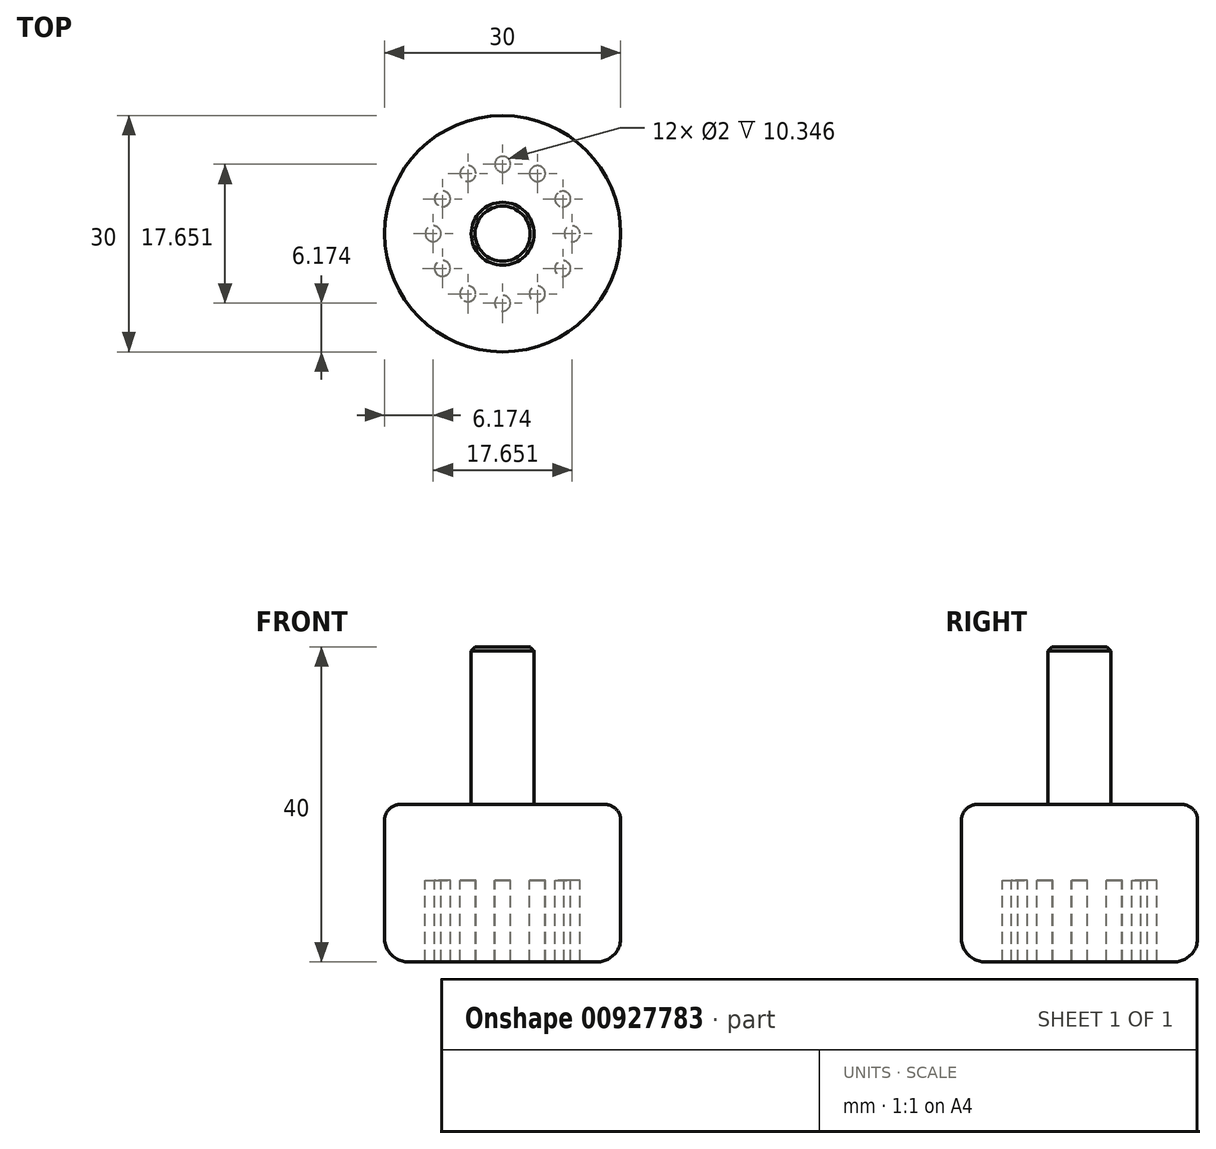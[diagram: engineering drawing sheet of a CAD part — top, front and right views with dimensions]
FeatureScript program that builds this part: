
annotation { "Feature Type Name" : "Feature", "Feature Type Description" : "" }
export const myFeature = defineFeature(function(context is Context, id is Id, definition is map)
    precondition{}
    {
        {
            var Q0;
            Q0=qCreatedBy(makeId("Top.planeOp"),FACE);
            cPlane(context, id + "F0", {"entities" : qUnion([Q0]), "cplaneType" : CPlaneType.OFFSET, "offset" : 83.57 * mm, "width" : 152.4 * mm, "height" : 152.4 * mm});
        }
        {
            var Q0;
            Q0=qCreatedBy(makeId("Front.planeOp"),FACE);
            var sketch = newSketch(context, id + "F1", { "sketchPlane" : qUnion([Q0])});
            skLineSegment(sketch, "E0", {"start": v(8.85, 83.91) * mm, "end": v(8.85, 47.77) * mm});
            skSolve(sketch);
        }
        {
            var Q0;
            Q0=qCreatedBy(id+"F0.planeOp",FACE);
            var sketch = newSketch(context, id + "F2", { "sketchPlane" : qUnion([Q0])});
            skCircle(sketch, "E1", {"center": v(8.83, -0.01) * mm, "radius": 1 * mm});
            skSolve(sketch);
        }
        {
            var Q0;
            Q0=makeQuery(id+"F2.imprint","IMPRINT",FACE,{"disambiguationData":[TD([[makeQuery(id+"F2.imprint","IMPRINT",EDGE,{"derivedFrom":sQuery(id+"F2.wireOp",EDGE,"E1")}),1.0]])]});
            var Q1;
            Q1=sQuery(id+"F1.wireOp",EDGE,"E0");
            var Q2;
            Q2=sQuery(id+"F1.wireOp",EDGE,"10137925-59a1-47c4-baab-5b0ec24871b5");
            sweep(context, id + "F3", {"profiles" : qUnion([Q0]), "path" : qUnion([Q1, Q2])});
        }
        {
            var Q0;
            Q0=qCreatedBy(makeId("Front.planeOp"),FACE);
            var sketch = newSketch(context, id + "F4", { "sketchPlane" : qUnion([Q0])});
            skLineSegment(sketch, "E2", {"start": v(0, 0) * mm, "end": v(0, 81.13) * mm, "construction": true});
            skSolve(sketch);
        }
        {
            var Q0;
            Q0=makeQuery(id+"F3.opSweep","SWEPT_BODY",BODY,{"disambiguationData":[OSD([sQuery(id+"F1.wireOp",EDGE,"10137925-59a1-47c4-baab-5b0ec24871b5"),sQuery(id+"F2.wireOp",EDGE,"E1")])]});
            var Q1;
            Q1=sQuery(id+"F4.wireOp",EDGE,"E2");
            circularPattern(context, id + "F5", {"entities" : qUnion([Q0]), "axis" : qUnion([Q1]), "angle" : 360 * degree, "instanceCount" : 12, "equalSpace" : true});
        }
        {
            var Q0;
            Q0=qCreatedBy(id+"F0.planeOp",FACE);
            var sketch = newSketch(context, id + "F6", { "sketchPlane" : qUnion([Q0])});
            skCircle(sketch, "E3", {"center": v(0, 0) * mm, "radius": 15 * mm});
            skSolve(sketch);
        }
        {
            var Q0;
            Q0=makeQuery(id+"F6.imprint","IMPRINT",FACE,{"disambiguationData":[TD([[makeQuery(id+"F6.imprint","IMPRINT",EDGE,{"derivedFrom":sQuery(id+"F6.wireOp",EDGE,"E3")}),1.0]])]});
            extrude(context, id + "F7", {"entities" : qUnion([Q0]), "endBound" : BoundingType.SYMMETRIC, "depth" : 20 * mm, "offsetDistance" : 25 * mm});
        }
        {
            var Q0;
            Q0=makeQuery(id+"F7.opExtrude","CAP_EDGE",EDGE,{"disambiguationData":[OSD([sQuery(id+"F6.wireOp",EDGE,"E3")])],"isStart":true});
            fillet(context, id + "F8", {"entities" : qUnion([Q0]), "radius" : 3 * mm, "tangentPropagation" : true, "allowEdgeOverflow" : false});
        }
        {
            var Q0;
            Q0=makeQuery(id+"F7.opExtrude","CAP_EDGE",EDGE,{"disambiguationData":[OSD([sQuery(id+"F6.wireOp",EDGE,"E3")])],"isStart":false});
            fillet(context, id + "F9", {"entities" : qUnion([Q0]), "radius" : 2 * mm, "tangentPropagation" : true, "allowEdgeOverflow" : false});
        }
        {
            var Q0;
            Q0=makeQuery(id+"F3.opSweep","SWEPT_BODY",BODY,{"disambiguationData":[OSD([sQuery(id+"F1.wireOp",EDGE,"E0"),sQuery(id+"F2.wireOp",EDGE,"E1")])]});
            var Q1;
            Q1=makeQuery(id+"F5.opPattern","COPY",BODY,{"derivedFrom":makeQuery(id+"F3.opSweep","SWEPT_BODY",BODY,{"disambiguationData":[OSD([sQuery(id+"F1.wireOp",EDGE,"E0"),sQuery(id+"F2.wireOp",EDGE,"E1")])]}),"instanceName":"1"});
            var Q2;
            Q2=makeQuery(id+"F5.opPattern","COPY",BODY,{"derivedFrom":makeQuery(id+"F3.opSweep","SWEPT_BODY",BODY,{"disambiguationData":[OSD([sQuery(id+"F1.wireOp",EDGE,"E0"),sQuery(id+"F2.wireOp",EDGE,"E1")])]}),"instanceName":"2"});
            var Q3;
            Q3=makeQuery(id+"F5.opPattern","COPY",BODY,{"derivedFrom":makeQuery(id+"F3.opSweep","SWEPT_BODY",BODY,{"disambiguationData":[OSD([sQuery(id+"F1.wireOp",EDGE,"E0"),sQuery(id+"F2.wireOp",EDGE,"E1")])]}),"instanceName":"3"});
            var Q4;
            Q4=makeQuery(id+"F5.opPattern","COPY",BODY,{"derivedFrom":makeQuery(id+"F3.opSweep","SWEPT_BODY",BODY,{"disambiguationData":[OSD([sQuery(id+"F1.wireOp",EDGE,"E0"),sQuery(id+"F2.wireOp",EDGE,"E1")])]}),"instanceName":"4"});
            var Q5;
            Q5=makeQuery(id+"F5.opPattern","COPY",BODY,{"derivedFrom":makeQuery(id+"F3.opSweep","SWEPT_BODY",BODY,{"disambiguationData":[OSD([sQuery(id+"F1.wireOp",EDGE,"E0"),sQuery(id+"F2.wireOp",EDGE,"E1")])]}),"instanceName":"5"});
            var Q6;
            Q6=makeQuery(id+"F5.opPattern","COPY",BODY,{"derivedFrom":makeQuery(id+"F3.opSweep","SWEPT_BODY",BODY,{"disambiguationData":[OSD([sQuery(id+"F1.wireOp",EDGE,"E0"),sQuery(id+"F2.wireOp",EDGE,"E1")])]}),"instanceName":"6"});
            var Q7;
            Q7=makeQuery(id+"F5.opPattern","COPY",BODY,{"derivedFrom":makeQuery(id+"F3.opSweep","SWEPT_BODY",BODY,{"disambiguationData":[OSD([sQuery(id+"F1.wireOp",EDGE,"E0"),sQuery(id+"F2.wireOp",EDGE,"E1")])]}),"instanceName":"7"});
            var Q8;
            Q8=makeQuery(id+"F5.opPattern","COPY",BODY,{"derivedFrom":makeQuery(id+"F3.opSweep","SWEPT_BODY",BODY,{"disambiguationData":[OSD([sQuery(id+"F1.wireOp",EDGE,"E0"),sQuery(id+"F2.wireOp",EDGE,"E1")])]}),"instanceName":"8"});
            var Q9;
            Q9=makeQuery(id+"F5.opPattern","COPY",BODY,{"derivedFrom":makeQuery(id+"F3.opSweep","SWEPT_BODY",BODY,{"disambiguationData":[OSD([sQuery(id+"F1.wireOp",EDGE,"E0"),sQuery(id+"F2.wireOp",EDGE,"E1")])]}),"instanceName":"9"});
            var Q10;
            Q10=makeQuery(id+"F5.opPattern","COPY",BODY,{"derivedFrom":makeQuery(id+"F3.opSweep","SWEPT_BODY",BODY,{"disambiguationData":[OSD([sQuery(id+"F1.wireOp",EDGE,"E0"),sQuery(id+"F2.wireOp",EDGE,"E1")])]}),"instanceName":"10"});
            var Q11;
            Q11=makeQuery(id+"F5.opPattern","COPY",BODY,{"derivedFrom":makeQuery(id+"F3.opSweep","SWEPT_BODY",BODY,{"disambiguationData":[OSD([sQuery(id+"F1.wireOp",EDGE,"E0"),sQuery(id+"F2.wireOp",EDGE,"E1")])]}),"instanceName":"11"});
            var Q12;
            Q12=makeQuery(id+"F7.opExtrude","SWEPT_BODY",BODY,{"disambiguationData":[OSD([sQuery(id+"F6.wireOp",EDGE,"E3")])]});
            booleanBodies(context, id + "F10", {"operationType" : BooleanOperationType.SUBTRACTION, "tools" : qUnion([Q0, Q1, Q2, Q3, Q4, Q5, Q6, Q7, Q8, Q9, Q10, Q11]), "targets" : qUnion([Q12])});
        }
        {
            var Q0;
            Q0=makeQuery(id+"F7.opExtrude","CAP_FACE",FACE,{"disambiguationData":[OSD([sQuery(id+"F6.wireOp",EDGE,"E3")])],"isStart":false});
            var sketch = newSketch(context, id + "F11", { "sketchPlane" : qUnion([Q0])});
            skCircle(sketch, "E4", {"center": v(0, 0) * mm, "radius": 4 * mm});
            skSolve(sketch);
        }
        {
            var Q0;
            Q0=makeQuery(id+"F11.imprint","IMPRINT",FACE,{"disambiguationData":[TD([[makeQuery(id+"F11.imprint","IMPRINT",EDGE,{"derivedFrom":sQuery(id+"F11.wireOp",EDGE,"E4")}),1.0]])]});
            var Q1;
            Q1=sQuery(id+"F11.wireOp",EDGE,"E4");
            extrude(context, id + "F12", {"entities" : qUnion([Q0]), "operationType" : NewBodyOperationType.ADD, "surfaceEntities" : qUnion([Q1]), "depth" : 20 * mm, "offsetDistance" : 25 * mm});
        }
        {
            var Q0;
            Q0=makeQuery(id+"F12.opExtrude","CAP_EDGE",EDGE,{"disambiguationData":[OSD([sQuery(id+"F11.wireOp",EDGE,"E4")])],"isStart":false});
            chamfer(context, id + "F13", {"entities" : qUnion([Q0]), "width" : 0.5 * mm, "tangentPropagation" : true});
        }
    });
